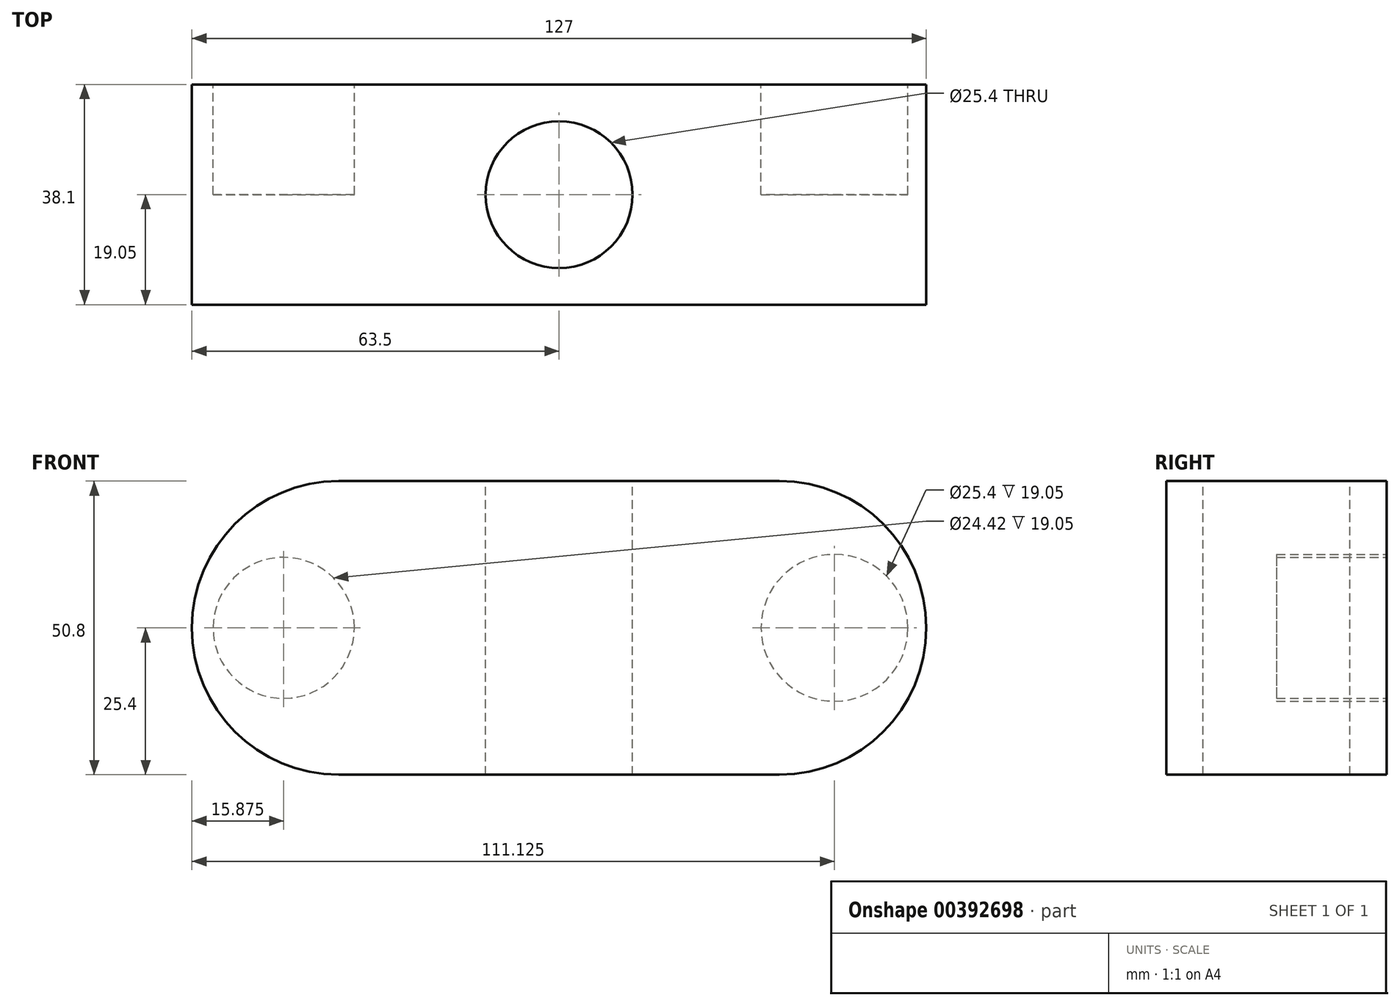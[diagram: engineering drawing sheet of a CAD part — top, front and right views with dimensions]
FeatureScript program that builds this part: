
annotation { "Feature Type Name" : "Feature", "Feature Type Description" : "" }
export const myFeature = defineFeature(function(context is Context, id is Id, definition is map)
    precondition{}
    {
        {
            var Q0;
            Q0=qCreatedBy(makeId("Front.planeOp"),FACE);
            var sketch = newSketch(context, id + "F0", { "sketchPlane" : qUnion([Q0])});
            skLineSegment(sketch, "E0.bottom", {"start": v(63.5, 25.4) * mm, "end": v(-63.5, 25.4) * mm});
            skLineSegment(sketch, "E0.top", {"start": v(63.5, -25.4) * mm, "end": v(-63.5, -25.4) * mm});
            skLineSegment(sketch, "E0.left", {"start": v(63.5, -25.4) * mm, "end": v(63.5, 25.4) * mm});
            skLineSegment(sketch, "E0.right", {"start": v(-63.5, -25.4) * mm, "end": v(-63.5, 25.4) * mm});
            skPoint(sketch, "E0.middle", {"position": v(0, 0) * mm});
            skSolve(sketch);
        }
        {
            var Q0;
            Q0 = qSketchRegion(id + "F0", true);
            extrude(context, id + "F1", {"entities" : qUnion([Q0]), "depth" : 38.1 * mm});
        }
        {
            var Q0;
            Q0=makeQuery(id+"F1.opExtrude","SWEPT_EDGE",EDGE,{"disambiguationData":[OSD([sQuery(id+"F0.wireOp",EDGE,"E0.bottom"),sQuery(id+"F0.wireOp",EDGE,"E0.left")])]});
            var Q1;
            Q1=makeQuery(id+"F1.opExtrude","SWEPT_EDGE",EDGE,{"disambiguationData":[OSD([sQuery(id+"F0.wireOp",EDGE,"E0.top"),sQuery(id+"F0.wireOp",EDGE,"E0.left")])]});
            var Q2;
            Q2=makeQuery(id+"F1.opExtrude","SWEPT_EDGE",EDGE,{"disambiguationData":[OSD([sQuery(id+"F0.wireOp",EDGE,"E0.bottom"),sQuery(id+"F0.wireOp",EDGE,"E0.right")])]});
            var Q3;
            Q3=makeQuery(id+"F1.opExtrude","SWEPT_EDGE",EDGE,{"disambiguationData":[OSD([sQuery(id+"F0.wireOp",EDGE,"E0.top"),sQuery(id+"F0.wireOp",EDGE,"E0.right")])]});
            fillet(context, id + "F2", {"entities" : qUnion([Q0, Q1, Q2, Q3]), "radius" : 25.4 * mm, "tangentPropagation" : true, "allowEdgeOverflow" : false});
        }
        {
            var Q0;
            Q0=makeQuery(id+"F1.opExtrude","CAP_FACE",FACE,{"disambiguationData":[OSD([sQuery(id+"F0.wireOp",EDGE,"E0.bottom"),sQuery(id+"F0.wireOp",EDGE,"E0.top"),sQuery(id+"F0.wireOp",EDGE,"E0.left"),sQuery(id+"F0.wireOp",EDGE,"E0.right")])],"isStart":true});
            var sketch = newSketch(context, id + "F3", { "sketchPlane" : qUnion([Q0])});
            skCircle(sketch, "E1", {"center": v(47.62, 0) * mm, "radius": 12.2 * mm});
            skCircle(sketch, "E2", {"center": v(-47.62, 0) * mm, "radius": 12.7 * mm});
            skSolve(sketch);
        }
        {
            var Q0;
            Q0 = qSketchRegion(id + "F3", true);
            extrude(context, id + "F4", {"entities" : qUnion([Q0]), "operationType" : NewBodyOperationType.REMOVE, "oppositeDirection" : true, "depth" : 19.05 * mm});
        }
        {
            var Q0;
            Q0=makeQuery(id+"F1.opExtrude","SWEPT_FACE",FACE,{"disambiguationData":[OSD([sQuery(id+"F0.wireOp",EDGE,"E0.bottom")])]});
            var sketch = newSketch(context, id + "F5", { "sketchPlane" : qUnion([Q0])});
            skCircle(sketch, "E3", {"center": v(0, -19.05) * mm, "radius": 12.7 * mm});
            skSolve(sketch);
        }
        {
            var Q0;
            Q0 = qSketchRegion(id + "F5", true);
            extrude(context, id + "F6", {"entities" : qUnion([Q0]), "operationType" : NewBodyOperationType.REMOVE, "oppositeDirection" : true, "depth" : 50.8 * mm});
        }
    });
